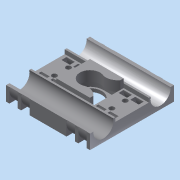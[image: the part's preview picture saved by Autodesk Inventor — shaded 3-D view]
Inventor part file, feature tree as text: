
AUTODESK INVENTOR PART (.ipt)
format: ipt  version: 2015 (Build 190159000, 159)  size: 368,128 bytes
history: native  units: in
note: dims shown in document units (in); Inventor stores cm internally (conversion verified against a paired STEP export)
features: sketch x15, extrude x10, hole x3, projected_geometry x3, pattern_linear x2, revolve x1
ambient origin geometry x8: Origin, YZ Plane, XZ Plane, XY Plane, X Axis, Y Axis, Z Axis, Center Point
bodies: Solid1 (feature_tree)
feature tree (34):
  sketch  "Sketch1"  dims[d0=0.7874in d1=0.7874in]
  extrude  "Extrusion1"  Depth=0.7874in
  hole  "Hole1"  [1 undecoded]
  extrude  "Extrusion2"  Depth=0.3937in
  extrude  "Extrusion3"  Depth=0.0787in
  extrude  "Extrusion4"  Depth=0.3in
  hole  "Hole2"  [1 undecoded]
  extrude  "Extrusion5"  Depth=0.1575in TaperAngle=0.0deg
  hole  "Hole3"  [1 undecoded]
  extrude  "Extrusion6"  Depth=0.5906in
  extrude  "Extrusion7"  Depth=0.4724in
  sketch  "Sketch12"  dims[d39=0.2362in d40=0.2362in]
  extrude  "Extrusion9"  Depth=0.4724in
  extrude  "Extrusion10"  Depth=0.2362in
  extrude  "Extrusion11"  Depth=0.315in TaperAngle=0.0deg
  revolve  "Revolution1"  [1 undecoded]
  pattern_linear  "Rectangular Pattern2"  Spacing1=0.2362in  [1 undecoded]
  pattern_linear  "Rectangular Pattern3"  Spacing1=0.315in  [1 undecoded]
  sketch  "Sketch2"  dims[d2=0.3937in d3=0.2362in d4=0.0in]
  sketch  "Sketch3"  dims[d5=0.4724in d6=0.75in d7=0.375in d8=0.25in d9=0.5635in d10=1.0in d11=0.8108in d12=0.3937in]
  sketch  "Sketch4"  dims[d13=0.0787in d14=0.0787in]
  sketch  "Sketch5"  dims[d16=0.3in d17=0.3in]
  sketch  "Sketch6"  dims[d18=0.2362in d19=0.0in d20=0.6299in]
  sketch  "Sketch7"  dims[d21=0.1575in d22=0.0in d23=0.1575in d24=0.0in]
  sketch  "Sketch8"  dims[d25=0.5512in d26=0.75in d27=0.375in d28=0.25in d29=0.5635in d30=1.0in d31=0.8108in d32=1.9685in]
  sketch  "Sketch9"  dims[d33=1.9685in d34=0.5906in]
  sketch  "Sketch10"  dims[d35=0.5906in d36=0.4724in]
  sketch  "Sketch11"  dims[d37=0.315in d38=0.4724in]
  projected_geometry  "Projected Loop1"
  projected_geometry  "Projected Loop2"
  sketch  "Sketch13"  dims[d41=0.315in d42=1.0in d43=0.0in]
  sketch  "Sketch14"  dims[d44=0.315in d45=0.315in]
  projected_geometry  "Projected Loop3"
  sketch  "Sketch15"  dims[d46=0.2362in d47=0.2362in d48=0.1181in d49=0.75in d50=0.375in d51=0.25in d52=0.5635in d53=1.0in d54=0.8108in d55=0.315in d56=0.315in d57=0.0787in d58=1.0in d59=0.0in d60=0.1969in d61=0.0in d62=0.6693in d63=0.0787in d66=0.0394in d67=0.0in d68=0.0394in d69=0.0in d70=0.0394in d71=0.0in d79=0.2756in d80=0.0787in d81=0.1969in d82=90.0deg d83=0.7874in d85=0.2756in d86=0.7874in d88=1.3386in d89=0.1181in d90=0.0394in d91=0.7874in d93=1.3386in d94=0.2756in]
note: 6 required parameter values undecoded (feature->parameter linkage not recoverable at this tier; creation-order binding heuristic only, values carry confidence <= 0.55)